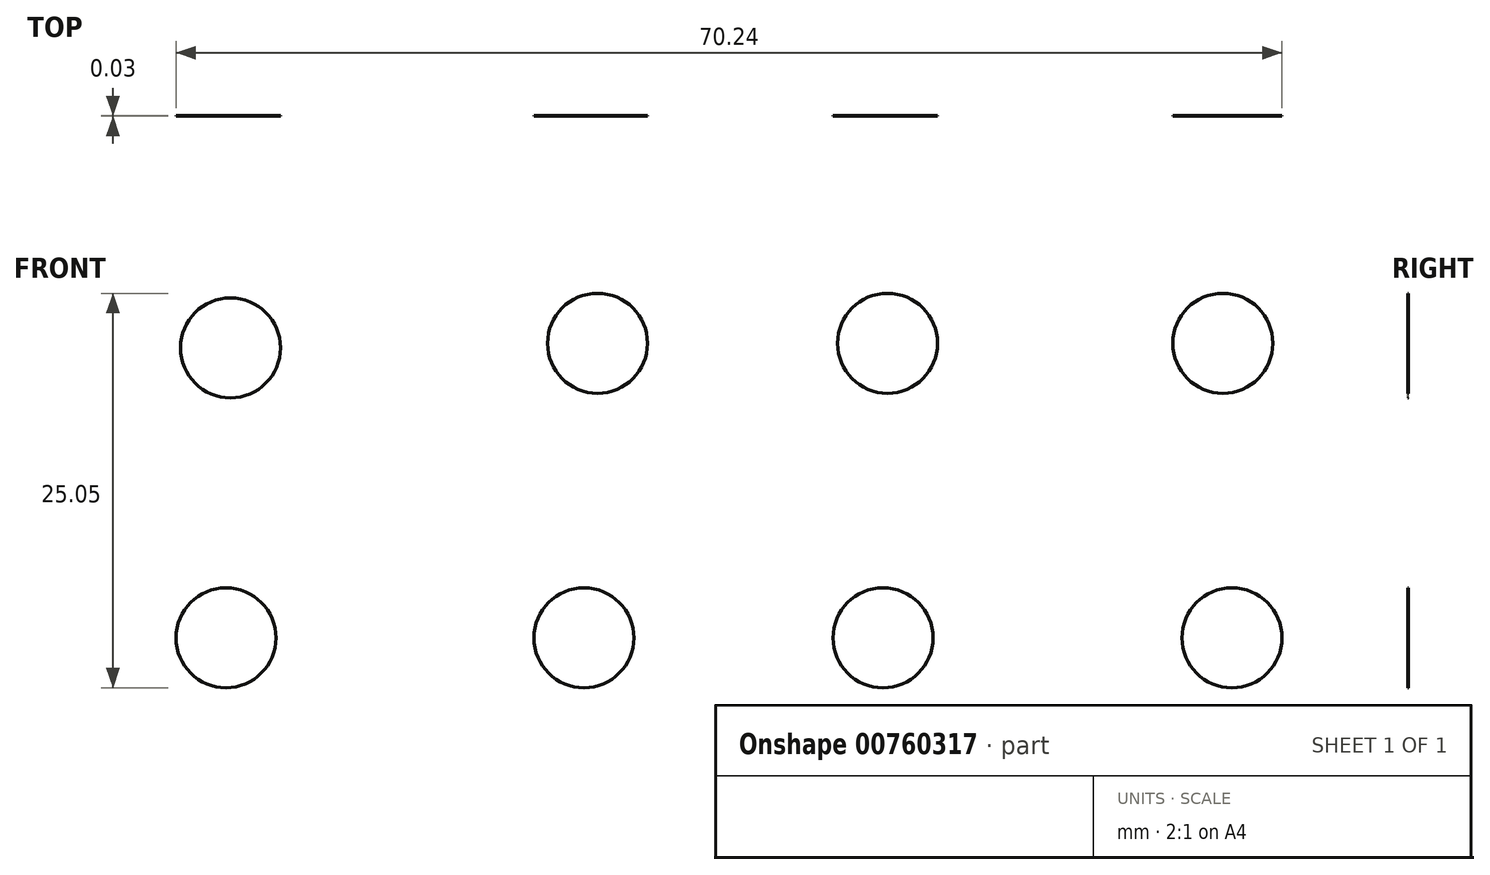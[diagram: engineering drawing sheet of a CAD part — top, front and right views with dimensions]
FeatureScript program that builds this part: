
annotation { "Feature Type Name" : "Feature", "Feature Type Description" : "" }
export const myFeature = defineFeature(function(context is Context, id is Id, definition is map)
    precondition{}
    {
        {
            var Q0;
            Q0=qCreatedBy(makeId("Front.planeOp"),FACE);
            var sketch = newSketch(context, id + "F0", { "sketchPlane" : qUnion([Q0])});
            skCircle(sketch, "E0", {"center": v(-57.5, 30.22) * mm, "radius": 3.18 * mm});
            skCircle(sketch, "E1", {"center": v(-34.2, 30.5) * mm, "radius": 3.17 * mm});
            skCircle(sketch, "E2", {"center": v(-57.8, 11.8) * mm, "radius": 3.18 * mm});
            skCircle(sketch, "E3", {"center": v(-35.06, 11.8) * mm, "radius": 3.18 * mm});
            skCircle(sketch, "E4", {"center": v(-16.06, 11.8) * mm, "radius": 3.18 * mm});
            skCircle(sketch, "E5", {"center": v(6.1, 11.8) * mm, "radius": 3.18 * mm});
            skCircle(sketch, "E6", {"center": v(-15.77, 30.5) * mm, "radius": 3.18 * mm});
            skCircle(sketch, "E7", {"center": v(5.52, 30.5) * mm, "radius": 3.18 * mm});
            skSolve(sketch);
        }
        {
            var Q0;
            Q0=makeQuery(id+"F0.imprint","IMPRINT",FACE,{"disambiguationData":[TD([[makeQuery(id+"F0.imprint","IMPRINT",EDGE,{"derivedFrom":sQuery(id+"F0.wireOp",EDGE,"E0")}),1.0]])]});
            var Q1;
            Q1=makeQuery(id+"F0.imprint","IMPRINT",FACE,{"disambiguationData":[TD([[makeQuery(id+"F0.imprint","IMPRINT",EDGE,{"derivedFrom":sQuery(id+"F0.wireOp",EDGE,"E1")}),1.0]])]});
            var Q2;
            Q2=makeQuery(id+"F0.imprint","IMPRINT",FACE,{"disambiguationData":[TD([[makeQuery(id+"F0.imprint","IMPRINT",EDGE,{"derivedFrom":sQuery(id+"F0.wireOp",EDGE,"E6")}),1.0]])]});
            var Q3;
            Q3=makeQuery(id+"F0.imprint","IMPRINT",FACE,{"disambiguationData":[TD([[makeQuery(id+"F0.imprint","IMPRINT",EDGE,{"derivedFrom":sQuery(id+"F0.wireOp",EDGE,"E7")}),1.0]])]});
            var Q4;
            Q4=makeQuery(id+"F0.imprint","IMPRINT",FACE,{"disambiguationData":[TD([[makeQuery(id+"F0.imprint","IMPRINT",EDGE,{"derivedFrom":sQuery(id+"F0.wireOp",EDGE,"E5")}),1.0]])]});
            var Q5;
            Q5=makeQuery(id+"F0.imprint","IMPRINT",FACE,{"disambiguationData":[TD([[makeQuery(id+"F0.imprint","IMPRINT",EDGE,{"derivedFrom":sQuery(id+"F0.wireOp",EDGE,"E4")}),1.0]])]});
            var Q6;
            Q6=makeQuery(id+"F0.imprint","IMPRINT",FACE,{"disambiguationData":[TD([[makeQuery(id+"F0.imprint","IMPRINT",EDGE,{"derivedFrom":sQuery(id+"F0.wireOp",EDGE,"E3")}),1.0]])]});
            var Q7;
            Q7=makeQuery(id+"F0.imprint","IMPRINT",FACE,{"disambiguationData":[TD([[makeQuery(id+"F0.imprint","IMPRINT",EDGE,{"derivedFrom":sQuery(id+"F0.wireOp",EDGE,"E2")}),1.0]])]});
            extrude(context, id + "F1", {"entities" : qUnion([Q0, Q1, Q2, Q3, Q4, Q5, Q6, Q7]), "depth" : 3 / 101.6 * mm, "offsetDistance" : 25.4 * mm});
        }
    });
